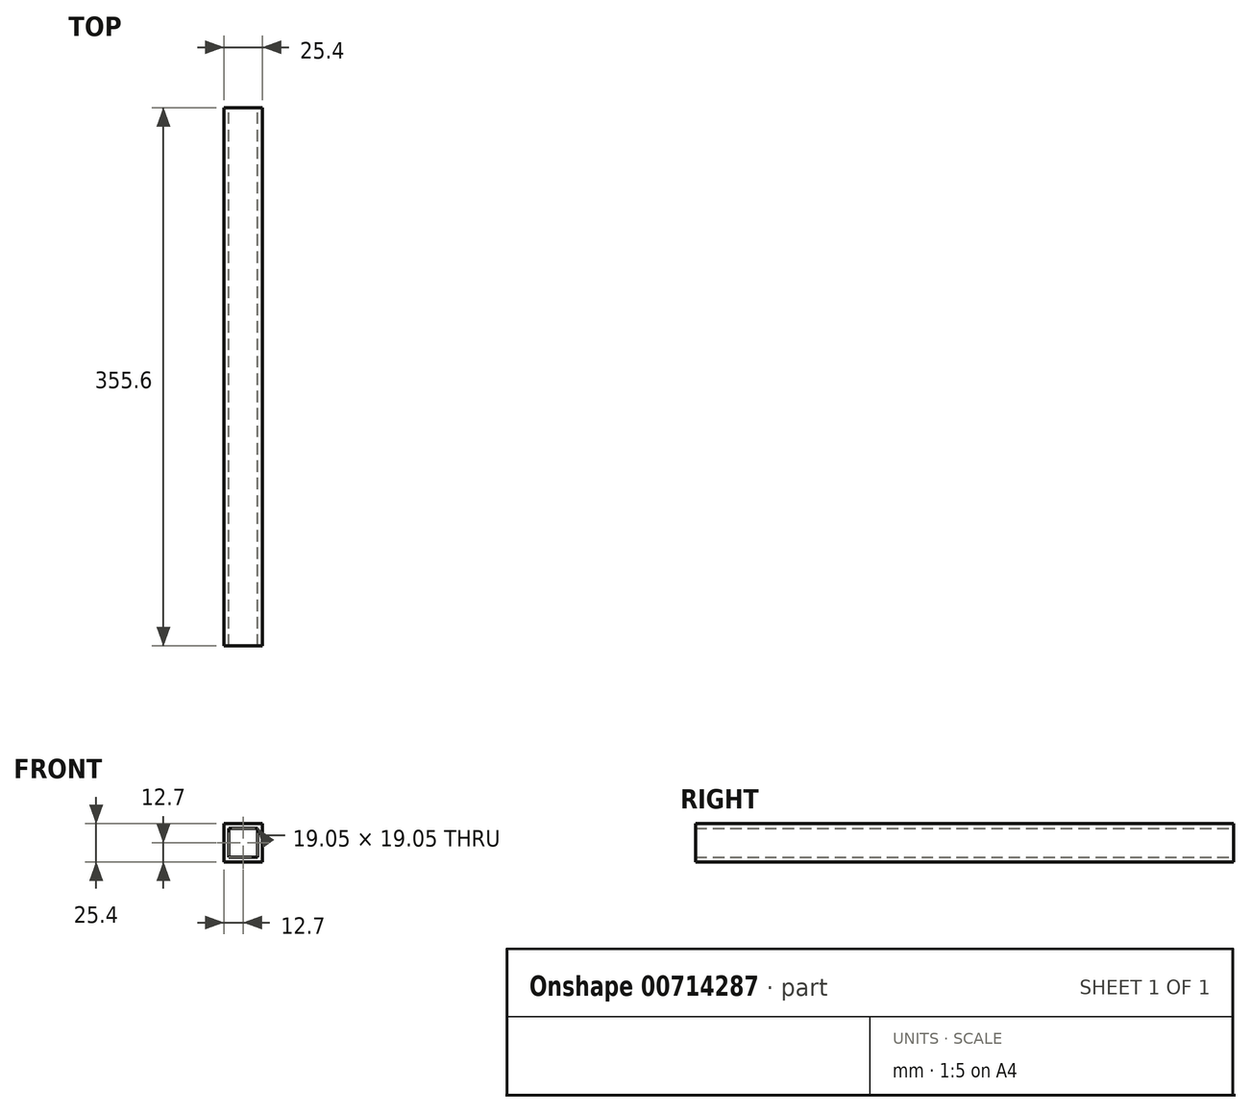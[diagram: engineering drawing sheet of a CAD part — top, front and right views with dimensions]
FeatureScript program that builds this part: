
annotation { "Feature Type Name" : "Feature", "Feature Type Description" : "" }
export const myFeature = defineFeature(function(context is Context, id is Id, definition is map)
    precondition{}
    {
        {
            var Q0;
            Q0=qCreatedBy(makeId("Front.planeOp"),FACE);
            var sketch = newSketch(context, id + "F0", { "sketchPlane" : qUnion([Q0])});
            skLineSegment(sketch, "E0.bottom", {"start": v(12.7, 12.7) * mm, "end": v(-12.7, 12.7) * mm});
            skLineSegment(sketch, "E0.top", {"start": v(12.7, -12.7) * mm, "end": v(-12.7, -12.7) * mm});
            skLineSegment(sketch, "E0.left", {"start": v(12.7, 12.7) * mm, "end": v(12.7, -12.7) * mm});
            skLineSegment(sketch, "E0.right", {"start": v(-12.7, 12.7) * mm, "end": v(-12.7, -12.7) * mm});
            skPoint(sketch, "E0.middle", {"position": v(0, 0) * mm});
            skLineSegment(sketch, "E1.0", {"start": v(9.53, -9.52) * mm, "end": v(-9.53, -9.52) * mm});
            skLineSegment(sketch, "E1.1", {"start": v(9.53, 9.53) * mm, "end": v(9.53, -9.52) * mm});
            skLineSegment(sketch, "E1.2", {"start": v(9.53, 9.53) * mm, "end": v(-9.53, 9.53) * mm});
            skLineSegment(sketch, "E1.3", {"start": v(-9.53, 9.53) * mm, "end": v(-9.53, -9.52) * mm});
            skSolve(sketch);
        }
        {
            var Q0;
            Q0 = qSketchRegion(id + "F0", true);
            extrude(context, id + "F1", {"entities" : qUnion([Q0]), "depth" : 355.6 * mm, "offsetDistance" : 25.4 * mm});
        }
    });
